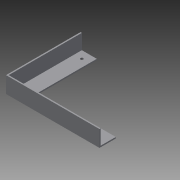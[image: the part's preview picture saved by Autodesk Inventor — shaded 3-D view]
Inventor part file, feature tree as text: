
AUTODESK INVENTOR PART (.ipt)
format: ipt  version: 2015 (Build 190159000, 159)  size: 132,608 bytes
history: native  units: in
note: dims shown in document units (in); Inventor stores cm internally (conversion verified against a paired STEP export)
features: extrude x2
ambient origin geometry x8: Origin, YZ Plane, XZ Plane, XY Plane, X Axis, Y Axis, Z Axis, Center Point
bodies: Body1 (feature_tree)
feature tree (2):
  extrude  "Extrusion6"  Depth=25.5906in
  extrude  "Extrusion7"  Depth=25.5906in
